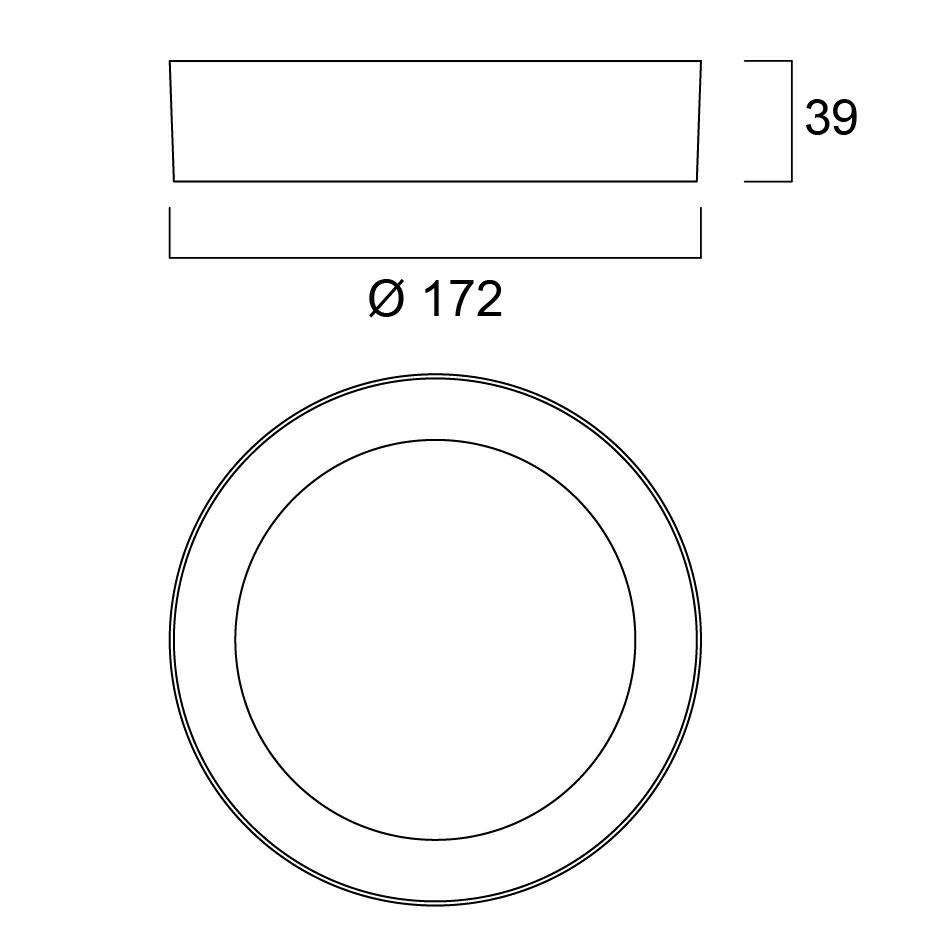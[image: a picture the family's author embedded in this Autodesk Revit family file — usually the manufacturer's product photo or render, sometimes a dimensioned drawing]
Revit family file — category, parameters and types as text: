
# Revit family: 0053906
name_source: partatom
category: Lighting Fixtures
revit_build: Autodesk Revit 2016 (Build: 20150220_1215(x64)
units: mm (PartAtom-declared; Revit-internal decimal feet)

## family parameters
Cut with Voids When Loaded = No
Host = Face
Light Source = Yes
OmniClass Number = 23.80.70.00
OmniClass Title = Lighting
Part Type = Normal
Room Calculation Point = No
Round Connector Dimension = Use Diameter
Shared = No

## types (1)
- 0053906 ST eco Downlight Flat 226 2075lm 840 DIM S
    Apparent Load = 20 VA
    Assembly Code = D5020200
    AssetType = Fixed
    ClassificationName = Uniclass2015
    ClassificationValue = EF_70_80
    Color Filter = 16777215
    Cost = 0 $
    Default Elevation = 1219 mm
    Description = Integrated LED surface mounted downlight providing 2220 fixture lumens at a wattage of 23W giving a high efficacy of 97lm/W. Fitting includes Leading/Trailing edge phase dimmable driver and has a round outer dimmension of of 226x226x39mm with an IP20 and IK02 rating providing uniform distribution with an Opal diffuser and 110° beam angle. Provided including a Loop in Loop out box and built with a white aluminium housing.
    Dimming Lamp Color Temperature Shift = <None>
    DimmingControlOptions = Dimmable
    DocumentationLiterature = http://www.sylvania-lighting.com
    DurationUnit = hours
    ElectricShockClassification = Class II
    Emit Shape Visible in Rendering = No
    Emit from Circle Diameter = 170 mm
    ExpectedLife = 50000
    IfcExportAs = IfcLightFixtureType
    IfcExportType = IfcLightFixtureType
    ImpactProtectionIndex = IK06
    IngressProtection = IP20
    InputNominalFrequency = 50/60 Hz
    InputVoltage = 220-240V~
    Keynote = 16500
    Lamp = LED
    LampColourRenderingIndex = 80
    LampColourTemperature = 4000 K
    LampNominalLuminous = 2075 lm
    LampsType = LED
    LuminousEfficacy = 103.7 lm/W
    Manufacturer = Feilo Sylvania
    ManufacturerName = Feilo Sylvania
    Material = aluminium housing, polystyrene diffuser
    Material_1_FEILO = Body-Sylvania-SylflatSurface-White
    Material_2_FEILO = LED-Sylvania-SylflatSurface
    Material_3_FEILO = <By Category>
    Material_4_FEILO = <By Category>
    Model = ST eco Downlight Flat 226 2075lm 840 DIM S
    ModelNumber = 0053906
    ModelReference = ST eco Downlight Flat 226 2075lm 840 DIM S
    Name = ST eco Downlight Flat 226 2075lm 840 DIM S
    NominalDepth = 226 mm  [stored 0.74147 ft]
    NominalHeight = 39 mm  [stored 0.127953 ft]
    NominalLength = 226 mm  [stored 0.74147 ft]
    Photometric Web File = 0053906.ies
    PowerConsumption = 20 W
    PowerFactor = 0.9
    RadiusDiffuser_FEILO = 7 mm  [stored 0.0229659 ft]
    RadiusSquare_FEILO = 10 mm  [stored 0.0328084 ft]
    Round_FEILO = Yes
    Square_FEILO = No
    Tilt Angle = -90.00°
    Type Image = <None>
    TypeName = ST eco Downlight Flat 226 2075lm 840 DIM S
    URL = http://www.sylvania-lighting.com
    Voltage = 230 V
    Weight = 6.75 kg
    WidthDiffuser_FEILO = 170 mm
    Width_FEILO = 226 mm  [stored 0.74147 ft]

note: [stored X ft] marks values corroborated as IEEE doubles in the binary element streams (Revit-internal decimal feet)

## geometry (parser evidence)
native form markers: Sweep x1
no freeform markers — native parametric forms only
